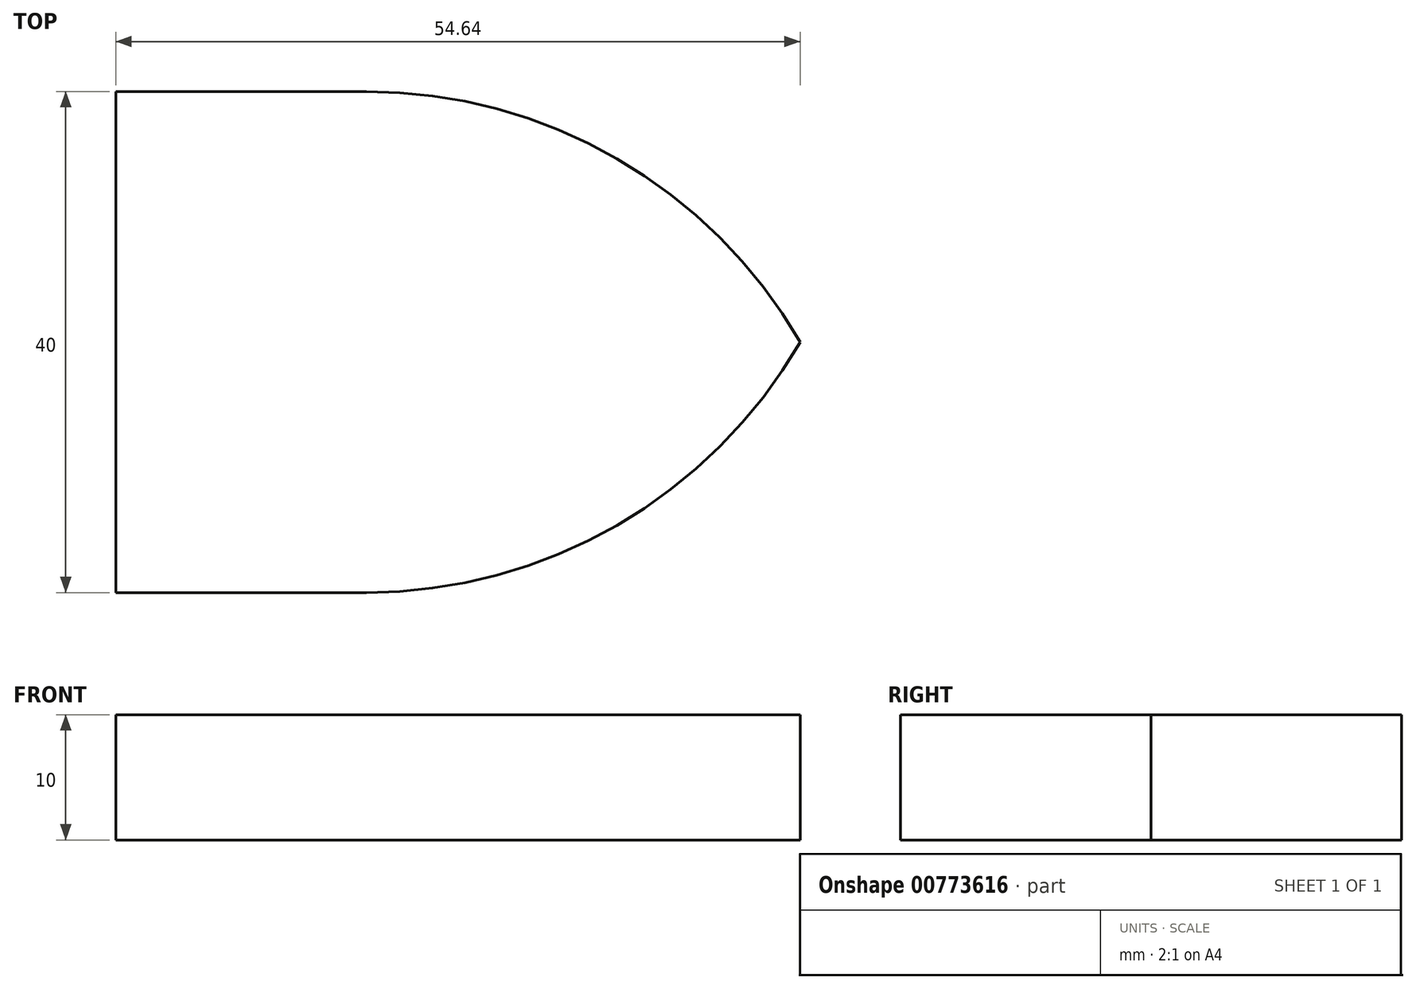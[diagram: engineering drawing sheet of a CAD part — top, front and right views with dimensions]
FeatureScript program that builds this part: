
annotation { "Feature Type Name" : "Feature", "Feature Type Description" : "" }
export const myFeature = defineFeature(function(context is Context, id is Id, definition is map)
    precondition{}
    {
        {
            var Q0;
            Q0=qCreatedBy(makeId("Front.planeOp"),FACE);
            var sketch = newSketch(context, id + "F0", { "sketchPlane" : qUnion([Q0])});
            skLineSegment(sketch, "E0.bottom", {"start": v(-27.3, -5.2) * mm, "end": v(32.7, -5.2) * mm});
            skLineSegment(sketch, "E0.top", {"start": v(-27.3, -15.2) * mm, "end": v(32.7, -15.2) * mm});
            skLineSegment(sketch, "E0.left", {"start": v(-27.3, -5.2) * mm, "end": v(-27.3, -15.2) * mm});
            skLineSegment(sketch, "E0.right", {"start": v(32.7, -5.2) * mm, "end": v(32.7, -15.2) * mm});
            skSolve(sketch);
        }
        {
            var Q0;
            Q0 = qSketchRegion(id + "F0", true);
            extrude(context, id + "F1", {"entities" : qUnion([Q0]), "depth" : 40 * mm, "offsetDistance" : 25 * mm});
        }
        {
            var Q0;
            Q0=makeQuery(id+"F1.opExtrude","CAP_EDGE",EDGE,{"disambiguationData":[OSD([sQuery(id+"F0.wireOp",EDGE,"E0.right")])],"isStart":false});
            var Q1;
            Q1=makeQuery(id+"F1.opExtrude","CAP_EDGE",EDGE,{"disambiguationData":[OSD([sQuery(id+"F0.wireOp",EDGE,"E0.right")])],"isStart":true});
            fillet(context, id + "F2", {"entities" : qUnion([Q0, Q1]), "radius" : 40 * mm, "tangentPropagation" : true, "allowEdgeOverflow" : false});
        }
    });
